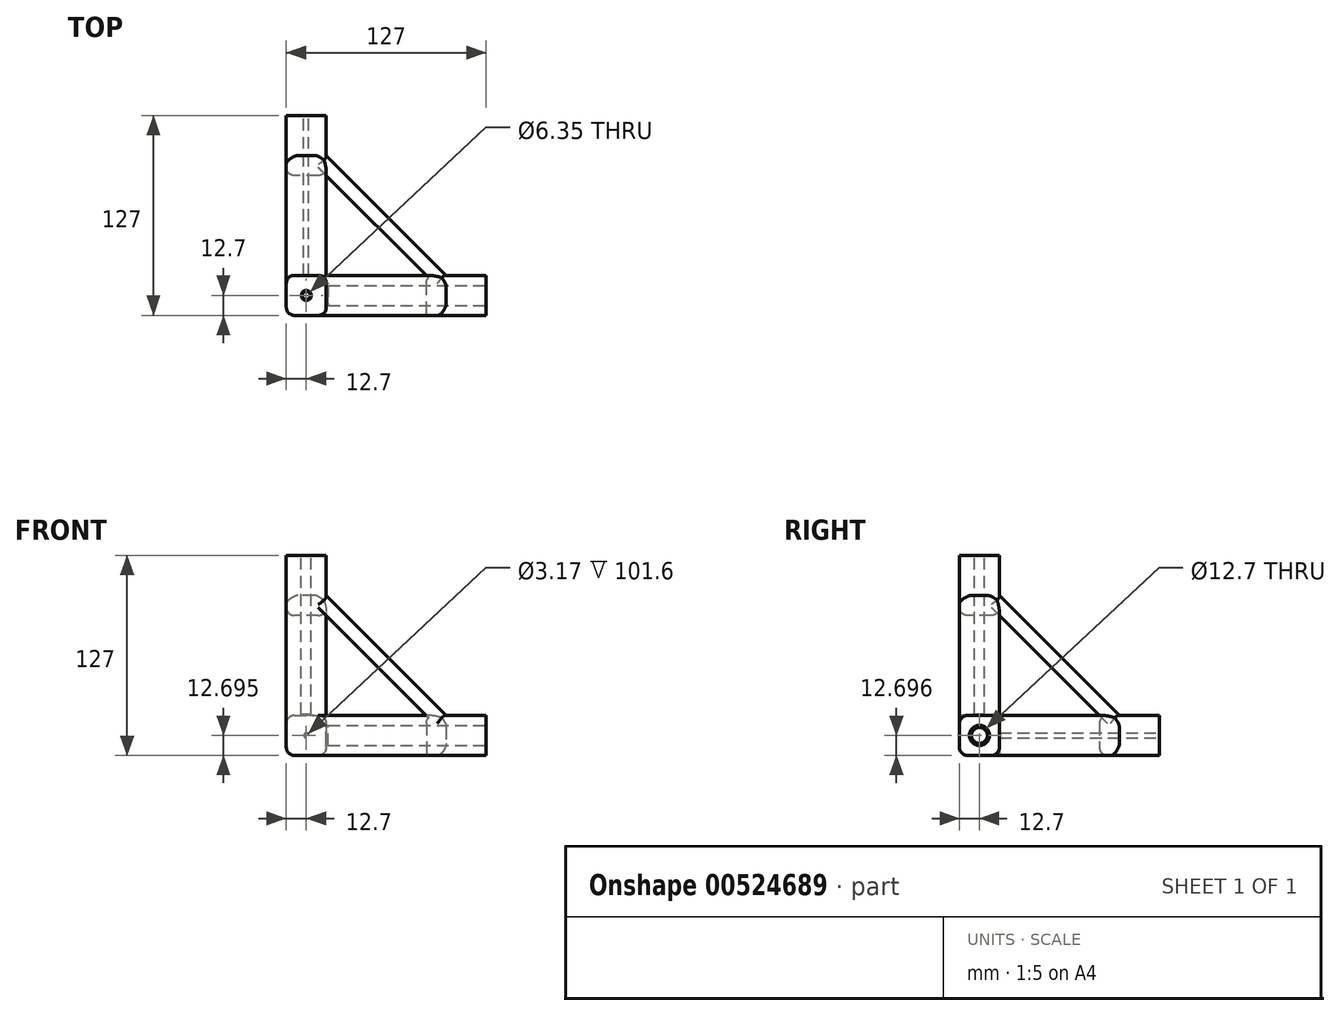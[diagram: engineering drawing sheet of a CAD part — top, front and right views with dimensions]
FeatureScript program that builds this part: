
annotation { "Feature Type Name" : "Feature", "Feature Type Description" : "" }
export const myFeature = defineFeature(function(context is Context, id is Id, definition is map)
    precondition{}
    {
        {
            var Q0;
            Q0=qCreatedBy(makeId("Top.planeOp"),FACE);
            var sketch = newSketch(context, id + "F0", { "sketchPlane" : qUnion([Q0])});
            skLineSegment(sketch, "E0.bottom", {"start": v(12.7, 12.7) * mm, "end": v(-12.7, 12.7) * mm});
            skLineSegment(sketch, "E0.top", {"start": v(12.7, -12.7) * mm, "end": v(-12.7, -12.7) * mm});
            skLineSegment(sketch, "E0.left", {"start": v(12.7, 12.7) * mm, "end": v(12.7, -12.7) * mm});
            skLineSegment(sketch, "E0.right", {"start": v(-12.7, 12.7) * mm, "end": v(-12.7, -12.7) * mm});
            skPoint(sketch, "E0.middle", {"position": v(0, 0) * mm});
            skSolve(sketch);
        }
        {
            var Q0;
            Q0=makeQuery(id+"F0.imprint","IMPRINT",FACE,{"disambiguationData":[TD([[makeQuery(id+"F0.imprint","IMPRINT",EDGE,{"derivedFrom":sQuery(id+"F0.wireOp",EDGE,"E0.bottom")}),1.0]])]});
            extrude(context, id + "F1", {"entities" : qUnion([Q0]), "depth" : 127 * mm, "offsetDistance" : 25.4 * mm});
        }
        {
            var Q0;
            Q0=makeQuery(id+"F1.opExtrude","SWEPT_FACE",FACE,{"disambiguationData":[OSD([sQuery(id+"F0.wireOp",EDGE,"E0.bottom")])]});
            var sketch = newSketch(context, id + "F2", { "sketchPlane" : qUnion([Q0])});
            skLineSegment(sketch, "E1.bottom", {"start": v(12.7, 0) * mm, "end": v(-12.7, 0) * mm});
            skLineSegment(sketch, "E1.top", {"start": v(12.7, 25.4) * mm, "end": v(-12.7, 25.4) * mm});
            skLineSegment(sketch, "E1.left", {"start": v(12.7, 0) * mm, "end": v(12.7, 25.4) * mm});
            skLineSegment(sketch, "E1.right", {"start": v(-12.7, 0) * mm, "end": v(-12.7, 25.4) * mm});
            skSolve(sketch);
        }
        {
            var Q0;
            Q0 = qSketchRegion(id + "F2", true);
            extrude(context, id + "F3", {"entities" : qUnion([Q0]), "operationType" : NewBodyOperationType.ADD, "depth" : 101.6 * mm, "offsetDistance" : 25.4 * mm});
        }
        {
            var Q0;
            Q0=makeQuery(id+"F3.boolean.opBoolean","MERGE",FACE,{"derivedFrom":[makeQuery(id+"F1.opExtrude","SWEPT_FACE",FACE,{"disambiguationData":[OSD([sQuery(id+"F0.wireOp",EDGE,"E0.left")])]}),makeQuery(id+"F3.opExtrude","SWEPT_FACE",FACE,{"disambiguationData":[OSD([sQuery(id+"F2.wireOp",EDGE,"E1.right")])]})]});
            var sketch = newSketch(context, id + "F4", { "sketchPlane" : qUnion([Q0])});
            skLineSegment(sketch, "E2.bottom", {"start": v(12.7, 25.4) * mm, "end": v(-12.7, 25.4) * mm});
            skLineSegment(sketch, "E2.top", {"start": v(12.7, 0) * mm, "end": v(-12.7, 0) * mm});
            skLineSegment(sketch, "E2.left", {"start": v(12.7, 25.4) * mm, "end": v(12.7, 0) * mm});
            skLineSegment(sketch, "E2.right", {"start": v(-12.7, 25.4) * mm, "end": v(-12.7, 0) * mm});
            skSolve(sketch);
        }
        {
            var Q0;
            Q0 = qSketchRegion(id + "F4", true);
            extrude(context, id + "F5", {"entities" : qUnion([Q0]), "operationType" : NewBodyOperationType.ADD, "depth" : 101.6 * mm, "offsetDistance" : 25.4 * mm});
        }
        {
            var Q0;
            Q0=makeQuery(id+"F3.opExtrude","CAP_FACE",FACE,{"disambiguationData":[OSD([sQuery(id+"F2.wireOp",EDGE,"E1.bottom"),sQuery(id+"F2.wireOp",EDGE,"E1.top"),sQuery(id+"F2.wireOp",EDGE,"E1.left"),sQuery(id+"F2.wireOp",EDGE,"E1.right")])],"isStart":false});
            var sketch = newSketch(context, id + "F6", { "sketchPlane" : qUnion([Q0])});
            skLineSegment(sketch, "E3", {"start": v(12.7, 0) * mm, "end": v(0, 0) * mm});
            skLineSegment(sketch, "E4", {"start": v(0, 0) * mm, "end": v(0, 12.7) * mm});
            skCircle(sketch, "E5", {"center": v(0, 12.7) * mm, "radius": 1.59 * mm});
            skSolve(sketch);
        }
        {
            var Q0;
            Q0 = qSketchRegion(id + "F6", true);
            extrude(context, id + "F7", {"entities" : qUnion([Q0]), "operationType" : NewBodyOperationType.REMOVE, "oppositeDirection" : true, "depth" : 101.6 * mm, "offsetDistance" : 25.4 * mm});
        }
        {
            var Q0;
            Q0=makeQuery(id+"F5.opExtrude","CAP_FACE",FACE,{"disambiguationData":[OSD([sQuery(id+"F4.wireOp",EDGE,"E2.bottom"),sQuery(id+"F4.wireOp",EDGE,"E2.top"),sQuery(id+"F4.wireOp",EDGE,"E2.left"),sQuery(id+"F4.wireOp",EDGE,"E2.right")])],"isStart":false});
            var sketch = newSketch(context, id + "F8", { "sketchPlane" : qUnion([Q0])});
            skLineSegment(sketch, "E6", {"start": v(12.7, 0) * mm, "end": v(0, 0) * mm});
            skLineSegment(sketch, "E7", {"start": v(0, 0) * mm, "end": v(0, 12.7) * mm});
            skCircle(sketch, "E8", {"center": v(0, 12.7) * mm, "radius": 6.35 * mm});
            skSolve(sketch);
        }
        {
            var Q0;
            Q0 = qSketchRegion(id + "F8", true);
            extrude(context, id + "F9", {"entities" : qUnion([Q0]), "operationType" : NewBodyOperationType.REMOVE, "oppositeDirection" : true, "depth" : 101.6 * mm, "offsetDistance" : 25.4 * mm});
        }
        {
            var Q0;
            Q0=makeQuery(id+"F1.opExtrude","CAP_FACE",FACE,{"disambiguationData":[OSD([sQuery(id+"F0.wireOp",EDGE,"E0.bottom"),sQuery(id+"F0.wireOp",EDGE,"E0.top"),sQuery(id+"F0.wireOp",EDGE,"E0.left"),sQuery(id+"F0.wireOp",EDGE,"E0.right")])],"isStart":false});
            var sketch = newSketch(context, id + "F10", { "sketchPlane" : qUnion([Q0])});
            skLineSegment(sketch, "E9", {"start": v(-12.7, 12.7) * mm, "end": v(0, 12.7) * mm});
            skLineSegment(sketch, "E10", {"start": v(0, 12.7) * mm, "end": v(0, 0) * mm});
            skCircle(sketch, "E11", {"center": v(0, 0) * mm, "radius": 3.18 * mm});
            skSolve(sketch);
        }
        {
            var Q0;
            Q0 = qSketchRegion(id + "F10", true);
            extrude(context, id + "F11", {"entities" : qUnion([Q0]), "operationType" : NewBodyOperationType.REMOVE, "oppositeDirection" : true, "depth" : 101.6 * mm, "offsetDistance" : 25.4 * mm});
        }
        {
            var Q0;
            Q0=makeQuery(id+"F3.boolean.opBoolean","MERGE",FACE,{"derivedFrom":[makeQuery(id+"F1.opExtrude","SWEPT_FACE",FACE,{"disambiguationData":[OSD([sQuery(id+"F0.wireOp",EDGE,"E0.right")])]}),makeQuery(id+"F3.opExtrude","SWEPT_FACE",FACE,{"disambiguationData":[OSD([sQuery(id+"F2.wireOp",EDGE,"E1.left")])]})]});
            var sketch = newSketch(context, id + "F12", { "sketchPlane" : qUnion([Q0])});
            skLineSegment(sketch, "E12", {"start": v(-12.7, 25.4) * mm, "end": v(-12.7, 101.6) * mm});
            skLineSegment(sketch, "E13", {"start": v(-12.7, 101.6) * mm, "end": v(-88.9, 25.4) * mm});
            skLineSegment(sketch, "E14", {"start": v(-88.9, 25.4) * mm, "end": v(-12.7, 25.4) * mm});
            skLineSegment(sketch, "E15", {"start": v(-88.9, 25.4) * mm, "end": v(-76.2, 25.4) * mm});
            skLineSegment(sketch, "E16", {"start": v(-76.2, 25.4) * mm, "end": v(-12.7, 88.9) * mm});
            skSolve(sketch);
        }
        {
            var Q0;
            {var subQ0=sQuery(id+"F12.wireOp",EDGE,"E13");Q0=makeQuery(id+"F12.imprint","IMPRINT",FACE,{"disambiguationData":[TD([[makeQuery(id+"F12.imprint","IMPRINT",EDGE,{"derivedFrom":subQ0}),1.0]])]});}
            extrude(context, id + "F13", {"entities" : qUnion([Q0]), "operationType" : NewBodyOperationType.ADD, "oppositeDirection" : true, "depth" : 25.4 * mm, "offsetDistance" : 25.4 * mm});
        }
        {
            var Q0;
            Q0=makeQuery(id+"F5.boolean.opBoolean","MERGE",FACE,{"derivedFrom":[makeQuery(id+"F3.boolean.opBoolean","MERGE",FACE,{"derivedFrom":[makeQuery(id+"F1.opExtrude","CAP_FACE",FACE,{"disambiguationData":[OSD([sQuery(id+"F0.wireOp",EDGE,"E0.bottom"),sQuery(id+"F0.wireOp",EDGE,"E0.top"),sQuery(id+"F0.wireOp",EDGE,"E0.left"),sQuery(id+"F0.wireOp",EDGE,"E0.right")])],"isStart":true}),makeQuery(id+"F3.opExtrude","SWEPT_FACE",FACE,{"disambiguationData":[OSD([sQuery(id+"F2.wireOp",EDGE,"E1.bottom")])]})]}),makeQuery(id+"F5.opExtrude","SWEPT_FACE",FACE,{"disambiguationData":[OSD([sQuery(id+"F4.wireOp",EDGE,"E2.top")])]})]});
            var sketch = newSketch(context, id + "F14", { "sketchPlane" : qUnion([Q0])});
            skLineSegment(sketch, "E17", {"start": v(12.7, -12.7) * mm, "end": v(88.9, -12.7) * mm});
            skLineSegment(sketch, "E18", {"start": v(88.9, -12.7) * mm, "end": v(12.7, -88.9) * mm});
            skLineSegment(sketch, "E19", {"start": v(12.7, -88.9) * mm, "end": v(12.7, -12.7) * mm});
            skLineSegment(sketch, "E20", {"start": v(12.7, -88.9) * mm, "end": v(12.7, -76.2) * mm});
            skLineSegment(sketch, "E21", {"start": v(12.7, -76.2) * mm, "end": v(76.2, -12.7) * mm});
            skLineSegment(sketch, "E22", {"start": v(76.2, -12.7) * mm, "end": v(88.9, -12.7) * mm});
            skSolve(sketch);
        }
        {
            var Q0;
            Q0=makeQuery(id+"F14.imprint","IMPRINT",FACE,{"disambiguationData":[TD([[makeQuery(id+"F14.imprint","IMPRINT",EDGE,{"derivedFrom":sQuery(id+"F14.wireOp",EDGE,"E18")}),-1.0]])]});
            var Q1;
            Q1=makeQuery(id+"F5.opExtrude","SWEPT_FACE",FACE,{"disambiguationData":[OSD([sQuery(id+"F4.wireOp",EDGE,"E2.bottom")])]});
            extrude(context, id + "F15", {"entities" : qUnion([Q0]), "operationType" : NewBodyOperationType.ADD, "endBound" : BoundingType.UP_TO_SURFACE, "oppositeDirection" : true, "depth" : 25.65 * mm, "endBoundEntityFace" : qUnion([Q1]), "offsetDistance" : 25.4 * mm});
        }
        {
            var Q0;
            Q0=makeQuery(id+"F5.boolean.opBoolean","MERGE",FACE,{"derivedFrom":[makeQuery(id+"F1.opExtrude","SWEPT_FACE",FACE,{"disambiguationData":[OSD([sQuery(id+"F0.wireOp",EDGE,"E0.top")])]}),makeQuery(id+"F5.opExtrude","SWEPT_FACE",FACE,{"disambiguationData":[OSD([sQuery(id+"F4.wireOp",EDGE,"E2.right")])]})]});
            var sketch = newSketch(context, id + "F16", { "sketchPlane" : qUnion([Q0])});
            skLineSegment(sketch, "E23", {"start": v(12.7, 25.4) * mm, "end": v(12.7, 101.6) * mm});
            skLineSegment(sketch, "E24", {"start": v(12.7, 101.6) * mm, "end": v(88.9, 25.4) * mm});
            skLineSegment(sketch, "E25", {"start": v(88.9, 25.4) * mm, "end": v(12.7, 25.4) * mm});
            skLineSegment(sketch, "E26", {"start": v(12.7, 101.6) * mm, "end": v(12.7, 88.9) * mm});
            skLineSegment(sketch, "E27", {"start": v(12.7, 88.9) * mm, "end": v(76.2, 25.4) * mm});
            skLineSegment(sketch, "E28", {"start": v(76.2, 25.4) * mm, "end": v(88.9, 25.4) * mm});
            skSolve(sketch);
        }
        {
            var Q0;
            Q0=makeQuery(id+"F16.imprint","IMPRINT",FACE,{"disambiguationData":[TD([[makeQuery(id+"F16.imprint","IMPRINT",EDGE,{"derivedFrom":sQuery(id+"F16.wireOp",EDGE,"E24")}),-1.0]])]});
            var Q1;
            {var subQ4=sQuery(id+"F0.wireOp",EDGE,"E0.bottom");Q1=makeQuery(id+"F15.boolean.opBoolean","SPLIT",FACE,{"disambiguationData":[TD([makeQuery(id+"F1.opExtrude","SWEPT_FACE",FACE,{"disambiguationData":[OSD([subQ4])]})])],"derivedFrom":makeQuery(id+"F5.opExtrude","SWEPT_FACE",FACE,{"disambiguationData":[OSD([sQuery(id+"F4.wireOp",EDGE,"E2.left")])]})});}
            extrude(context, id + "F17", {"entities" : qUnion([Q0]), "operationType" : NewBodyOperationType.ADD, "endBound" : BoundingType.UP_TO_SURFACE, "oppositeDirection" : true, "depth" : 11.43 * mm, "endBoundEntityFace" : qUnion([Q1]), "offsetDistance" : 25.4 * mm});
        }
        {
            var Q0;
            Q0=makeQuery(id+"F13.opExtrude","CAP_EDGE",EDGE,{"disambiguationData":[OSD([sQuery(id+"F12.wireOp",EDGE,"E13")])],"isStart":false});
            var Q1;
            Q1=makeQuery(id+"F13.opExtrude","CAP_EDGE",EDGE,{"disambiguationData":[OSD([sQuery(id+"F12.wireOp",EDGE,"E13")])],"isStart":true});
            fillet(context, id + "F18", {"entities" : qUnion([Q0, Q1]), "radius" : 7.62 * mm, "tangentPropagation" : true, "allowEdgeOverflow" : false});
        }
        {
            var Q0;
            Q0=makeQuery(id+"F15.opExtrude","CAP_EDGE",EDGE,{"disambiguationData":[OSD([sQuery(id+"F14.wireOp",EDGE,"E18")])],"isStart":false});
            var Q1;
            Q1=makeQuery(id+"F15.opExtrude","CAP_EDGE",EDGE,{"disambiguationData":[OSD([sQuery(id+"F14.wireOp",EDGE,"E18")])],"isStart":true});
            fillet(context, id + "F19", {"entities" : qUnion([Q0, Q1]), "radius" : 7.62 * mm, "tangentPropagation" : true, "allowEdgeOverflow" : false});
        }
        {
            var Q0;
            Q0=makeQuery(id+"F17.opExtrude","CAP_EDGE",EDGE,{"disambiguationData":[OSD([sQuery(id+"F16.wireOp",EDGE,"E24")])],"isStart":false});
            var Q1;
            Q1=makeQuery(id+"F17.opExtrude","CAP_EDGE",EDGE,{"disambiguationData":[OSD([sQuery(id+"F16.wireOp",EDGE,"E24")])],"isStart":true});
            fillet(context, id + "F20", {"entities" : qUnion([Q0, Q1]), "radius" : 7.62 * mm, "tangentPropagation" : true, "allowEdgeOverflow" : false});
        }
        {
            var Q0;
            Q0=makeQuery(id+"F9.boolean.opBoolean","COPY",EDGE,{"derivedFrom":makeQuery(id+"F9.opExtrude","CAP_EDGE",EDGE,{"disambiguationData":[OSD([sQuery(id+"F8.wireOp",EDGE,"E8")])],"isStart":false})});
            chamfer(context, id + "F21", {"entities" : qUnion([Q0]), "width" : 1.27 * mm, "tangentPropagation" : true});
        }
        {
            var Q0;
            Q0=makeQuery(id+"F11.boolean.opBoolean","COPY",EDGE,{"derivedFrom":makeQuery(id+"F11.opExtrude","CAP_EDGE",EDGE,{"disambiguationData":[OSD([sQuery(id+"F10.wireOp",EDGE,"E11")])],"isStart":false})});
            chamfer(context, id + "F22", {"entities" : qUnion([Q0]), "width" : 0.64 * mm, "tangentPropagation" : true});
        }
        {
            var Q0;
            Q0=makeQuery(id+"F3.boolean.opBoolean","MERGE",EDGE,{"derivedFrom":[makeQuery(id+"F1.opExtrude","CAP_EDGE",EDGE,{"disambiguationData":[OSD([sQuery(id+"F0.wireOp",EDGE,"E0.right")])],"isStart":true}),makeQuery(id+"F3.opExtrude","SWEPT_EDGE",EDGE,{"disambiguationData":[OSD([sQuery(id+"F2.wireOp",EDGE,"E1.bottom"),sQuery(id+"F2.wireOp",EDGE,"E1.left")])]})]});
            var Q1;
            {var subQ0=sQuery(id+"F2.wireOp",EDGE,"E1.right");var subQ1=sQuery(id+"F2.wireOp",EDGE,"E1.bottom");var subQ2=sQuery(id+"F0.wireOp",EDGE,"E0.left");Q1=makeQuery(id+"F15.boolean.opBoolean","SPLIT",EDGE,{"disambiguationData":[TD([makeQuery(id+"F5.opExtrude","SWEPT_FACE",FACE,{"disambiguationData":[OSD([sQuery(id+"F4.wireOp",EDGE,"E2.left")])]})])],"derivedFrom":makeQuery(id+"F3.boolean.opBoolean","MERGE",EDGE,{"derivedFrom":[makeQuery(id+"F1.opExtrude","CAP_EDGE",EDGE,{"disambiguationData":[OSD([subQ2])],"isStart":true}),makeQuery(id+"F3.opExtrude","SWEPT_EDGE",EDGE,{"disambiguationData":[OSD([subQ1,subQ0])]})]})});}
            var Q2;
            {var subQ0=sQuery(id+"F2.wireOp",EDGE,"E1.left");var subQ1=sQuery(id+"F0.wireOp",EDGE,"E0.right");var subQ3=sQuery(id+"F2.wireOp",EDGE,"E1.top");var subQ4=sQuery(id+"F0.wireOp",EDGE,"E0.bottom");Q2=makeQuery(id+"F13.boolean.opBoolean","SPLIT",EDGE,{"disambiguationData":[TD([makeQuery(id+"F1.opExtrude","SWEPT_FACE",FACE,{"disambiguationData":[OSD([subQ4])]})])],"derivedFrom":makeQuery(id+"F3.opExtrude","SWEPT_EDGE",EDGE,{"disambiguationData":[OSD([subQ4,subQ1,subQ3,subQ0])]})});}
            var Q3;
            {var subQ0=sQuery(id+"F2.wireOp",EDGE,"E1.right");var subQ2=sQuery(id+"F2.wireOp",EDGE,"E1.top");var subQ3=sQuery(id+"F0.wireOp",EDGE,"E0.left");var subQ4=sQuery(id+"F0.wireOp",EDGE,"E0.bottom");Q3=makeQuery(id+"F13.boolean.opBoolean","SPLIT",EDGE,{"disambiguationData":[TD([makeQuery(id+"F1.opExtrude","SWEPT_FACE",FACE,{"disambiguationData":[OSD([subQ4])]})])],"derivedFrom":makeQuery(id+"F3.opExtrude","SWEPT_EDGE",EDGE,{"disambiguationData":[OSD([subQ4,subQ3,subQ2,subQ0])]})});}
            var Q4;
            {var subQ0=sQuery(id+"F2.wireOp",EDGE,"E1.right");var subQ1=sQuery(id+"F12.wireOp",EDGE,"E13");var subQ2=sQuery(id+"F2.wireOp",EDGE,"E1.top");var subQ3=sQuery(id+"F0.wireOp",EDGE,"E0.left");Q4=makeQuery(id+"F13.boolean.opBoolean","SPLIT",EDGE,{"disambiguationData":[TD([makeQuery(id+"F13.opExtrude","SWEPT_FACE",FACE,{"disambiguationData":[OSD([subQ1])]})])],"derivedFrom":makeQuery(id+"F3.opExtrude","SWEPT_EDGE",EDGE,{"disambiguationData":[OSD([sQuery(id+"F0.wireOp",EDGE,"E0.bottom"),subQ3,subQ2,subQ0])]})});}
            var Q5;
            {var subQ0=sQuery(id+"F2.wireOp",EDGE,"E1.left");var subQ1=sQuery(id+"F0.wireOp",EDGE,"E0.right");var subQ2=sQuery(id+"F12.wireOp",EDGE,"E13");var subQ3=sQuery(id+"F2.wireOp",EDGE,"E1.top");Q5=makeQuery(id+"F13.boolean.opBoolean","SPLIT",EDGE,{"disambiguationData":[TD([makeQuery(id+"F13.opExtrude","SWEPT_FACE",FACE,{"disambiguationData":[OSD([subQ2])]})])],"derivedFrom":makeQuery(id+"F3.opExtrude","SWEPT_EDGE",EDGE,{"disambiguationData":[OSD([sQuery(id+"F0.wireOp",EDGE,"E0.bottom"),subQ1,subQ3,subQ0])]})});}
            var Q6;
            {var subQ0=sQuery(id+"F2.wireOp",EDGE,"E1.right");var subQ1=sQuery(id+"F2.wireOp",EDGE,"E1.bottom");var subQ2=sQuery(id+"F0.wireOp",EDGE,"E0.left");var subQ3=sQuery(id+"F14.wireOp",EDGE,"E18");Q6=makeQuery(id+"F15.boolean.opBoolean","SPLIT",EDGE,{"disambiguationData":[TD([makeQuery(id+"F15.opExtrude","SWEPT_FACE",FACE,{"disambiguationData":[OSD([subQ3])]})])],"derivedFrom":makeQuery(id+"F3.boolean.opBoolean","MERGE",EDGE,{"derivedFrom":[makeQuery(id+"F1.opExtrude","CAP_EDGE",EDGE,{"disambiguationData":[OSD([subQ2])],"isStart":true}),makeQuery(id+"F3.opExtrude","SWEPT_EDGE",EDGE,{"disambiguationData":[OSD([subQ1,subQ0])]})]})});}
            fillet(context, id + "F23", {"entities" : qUnion([Q0, Q1, Q2, Q3, Q4, Q5, Q6]), "radius" : 5.08 * mm, "tangentPropagation" : true, "allowEdgeOverflow" : false});
        }
        {
            var Q0;
            Q0=makeQuery(id+"F1.opExtrude","SWEPT_EDGE",EDGE,{"disambiguationData":[OSD([sQuery(id+"F0.wireOp",EDGE,"E0.top"),sQuery(id+"F0.wireOp",EDGE,"E0.right")])]});
            var Q1;
            {var subQ0=sQuery(id+"F0.wireOp",EDGE,"E0.right");var subQ2=sQuery(id+"F0.wireOp",EDGE,"E0.bottom");Q1=makeQuery(id+"F13.boolean.opBoolean","SPLIT",EDGE,{"disambiguationData":[TD([makeQuery(id+"F3.opExtrude","SWEPT_FACE",FACE,{"disambiguationData":[OSD([sQuery(id+"F2.wireOp",EDGE,"E1.top")])]})])],"derivedFrom":makeQuery(id+"F1.opExtrude","SWEPT_EDGE",EDGE,{"disambiguationData":[OSD([subQ2,subQ0])]})});}
            var Q2;
            {var subQ0=sQuery(id+"F0.wireOp",EDGE,"E0.left");var subQ2=sQuery(id+"F0.wireOp",EDGE,"E0.top");Q2=makeQuery(id+"F17.boolean.opBoolean","SPLIT",EDGE,{"disambiguationData":[TD([makeQuery(id+"F5.opExtrude","SWEPT_FACE",FACE,{"disambiguationData":[OSD([sQuery(id+"F4.wireOp",EDGE,"E2.bottom")])]})])],"derivedFrom":makeQuery(id+"F1.opExtrude","SWEPT_EDGE",EDGE,{"disambiguationData":[OSD([subQ2,subQ0])]})});}
            var Q3;
            {var subQ0=sQuery(id+"F0.wireOp",EDGE,"E0.right");var subQ1=sQuery(id+"F12.wireOp",EDGE,"E13");var subQ2=sQuery(id+"F0.wireOp",EDGE,"E0.bottom");Q3=makeQuery(id+"F13.boolean.opBoolean","SPLIT",EDGE,{"disambiguationData":[TD([makeQuery(id+"F13.opExtrude","SWEPT_FACE",FACE,{"disambiguationData":[OSD([subQ1])]})])],"derivedFrom":makeQuery(id+"F1.opExtrude","SWEPT_EDGE",EDGE,{"disambiguationData":[OSD([subQ2,subQ0])]})});}
            var Q4;
            {var subQ0=sQuery(id+"F12.wireOp",EDGE,"E13");var subQ1=sQuery(id+"F0.wireOp",EDGE,"E0.left");var subQ2=sQuery(id+"F0.wireOp",EDGE,"E0.bottom");Q4=makeQuery(id+"F13.boolean.opBoolean","SPLIT",EDGE,{"disambiguationData":[TD([makeQuery(id+"F13.opExtrude","SWEPT_FACE",FACE,{"disambiguationData":[OSD([subQ0])]})])],"derivedFrom":makeQuery(id+"F1.opExtrude","SWEPT_EDGE",EDGE,{"disambiguationData":[OSD([subQ2,subQ1])]})});}
            var Q5;
            {var subQ0=sQuery(id+"F0.wireOp",EDGE,"E0.left");var subQ1=sQuery(id+"F16.wireOp",EDGE,"E24");var subQ2=sQuery(id+"F0.wireOp",EDGE,"E0.top");Q5=makeQuery(id+"F17.boolean.opBoolean","SPLIT",EDGE,{"disambiguationData":[TD([makeQuery(id+"F17.opExtrude","SWEPT_FACE",FACE,{"disambiguationData":[OSD([subQ1])]})])],"derivedFrom":makeQuery(id+"F1.opExtrude","SWEPT_EDGE",EDGE,{"disambiguationData":[OSD([subQ2,subQ0])]})});}
            fillet(context, id + "F24", {"entities" : qUnion([Q0, Q1, Q2, Q3, Q4, Q5]), "radius" : 5.08 * mm, "tangentPropagation" : true, "allowEdgeOverflow" : false});
        }
        {
            var Q0;
            {var subQ0=sQuery(id+"F2.wireOp",EDGE,"E1.right");var subQ1=sQuery(id+"F4.wireOp",EDGE,"E2.bottom");var subQ2=sQuery(id+"F2.wireOp",EDGE,"E1.top");var subQ3=sQuery(id+"F0.wireOp",EDGE,"E0.left");var subQ4=sQuery(id+"F0.wireOp",EDGE,"E0.bottom");var subQ6=sQuery(id+"F4.wireOp",EDGE,"E2.left");Q0=makeQuery(id+"F15.boolean.opBoolean","SPLIT",EDGE,{"disambiguationData":[TD([makeQuery(id+"F1.opExtrude","SWEPT_FACE",FACE,{"disambiguationData":[OSD([subQ4])]})])],"derivedFrom":makeQuery(id+"F5.opExtrude","SWEPT_EDGE",EDGE,{"disambiguationData":[OSD([subQ4,subQ3,subQ2,subQ0,subQ1,subQ6])]})});}
            var Q1;
            {var subQ1=sQuery(id+"F0.wireOp",EDGE,"E0.left");var subQ2=sQuery(id+"F0.wireOp",EDGE,"E0.bottom");Q1=makeQuery(id+"F13.boolean.opBoolean","SPLIT",EDGE,{"disambiguationData":[TD([makeQuery(id+"F3.opExtrude","SWEPT_FACE",FACE,{"disambiguationData":[OSD([sQuery(id+"F2.wireOp",EDGE,"E1.top")])]})])],"derivedFrom":makeQuery(id+"F1.opExtrude","SWEPT_EDGE",EDGE,{"disambiguationData":[OSD([subQ2,subQ1])]})});}
            var Q2;
            {var subQ0=sQuery(id+"F4.wireOp",EDGE,"E2.left");var subQ1=sQuery(id+"F4.wireOp",EDGE,"E2.bottom");var subQ2=sQuery(id+"F14.wireOp",EDGE,"E18");Q2=makeQuery(id+"F15.boolean.opBoolean","SPLIT",EDGE,{"disambiguationData":[TD([makeQuery(id+"F15.opExtrude","SWEPT_FACE",FACE,{"disambiguationData":[OSD([subQ2])]})])],"derivedFrom":makeQuery(id+"F5.opExtrude","SWEPT_EDGE",EDGE,{"disambiguationData":[OSD([sQuery(id+"F0.wireOp",EDGE,"E0.bottom"),sQuery(id+"F0.wireOp",EDGE,"E0.left"),sQuery(id+"F2.wireOp",EDGE,"E1.top"),sQuery(id+"F2.wireOp",EDGE,"E1.right"),subQ1,subQ0])]})});}
            var Q3;
            {var subQ0=sQuery(id+"F4.wireOp",EDGE,"E2.right");var subQ1=sQuery(id+"F4.wireOp",EDGE,"E2.bottom");var subQ2=sQuery(id+"F0.wireOp",EDGE,"E0.top");var subQ3=sQuery(id+"F16.wireOp",EDGE,"E24");Q3=makeQuery(id+"F17.boolean.opBoolean","SPLIT",EDGE,{"disambiguationData":[TD([makeQuery(id+"F17.opExtrude","SWEPT_FACE",FACE,{"disambiguationData":[OSD([subQ3])]})])],"derivedFrom":makeQuery(id+"F5.opExtrude","SWEPT_EDGE",EDGE,{"disambiguationData":[OSD([subQ2,sQuery(id+"F0.wireOp",EDGE,"E0.left"),subQ1,subQ0])]})});}
            var Q4;
            {var subQ0=sQuery(id+"F4.wireOp",EDGE,"E2.top");var subQ1=sQuery(id+"F14.wireOp",EDGE,"E18");var subQ2=sQuery(id+"F4.wireOp",EDGE,"E2.left");var subQ3=sQuery(id+"F2.wireOp",EDGE,"E1.bottom");var subQ4=sQuery(id+"F0.wireOp",EDGE,"E0.left");Q4=makeQuery(id+"F15.boolean.opBoolean","SPLIT",EDGE,{"disambiguationData":[TD([makeQuery(id+"F15.opExtrude","SWEPT_FACE",FACE,{"disambiguationData":[OSD([subQ1])]})])],"derivedFrom":makeQuery(id+"F5.opExtrude","SWEPT_EDGE",EDGE,{"disambiguationData":[OSD([subQ4,subQ3,sQuery(id+"F2.wireOp",EDGE,"E1.right"),subQ0,subQ2])]})});}
            fillet(context, id + "F25", {"entities" : qUnion([Q0, Q1, Q2, Q3, Q4]), "radius" : 5.08 * mm, "tangentPropagation" : true, "allowEdgeOverflow" : false});
        }
    });
